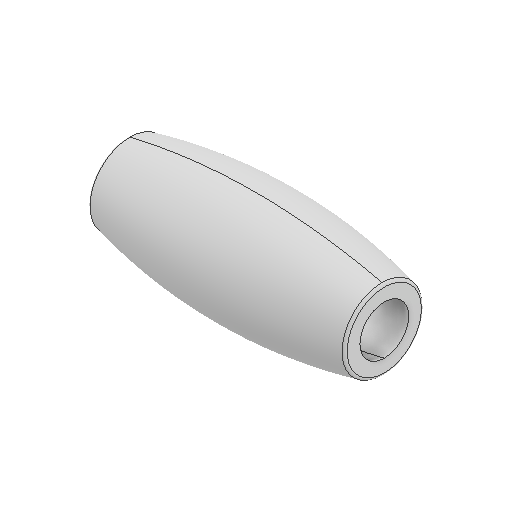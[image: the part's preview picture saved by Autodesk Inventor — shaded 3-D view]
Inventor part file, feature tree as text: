
AUTODESK INVENTOR PART (.ipt)
format: ipt  version: 2024.1 (Build 281209000, 209)  size: 181,248 bytes
history: native  units: in
note: dims shown in document units (in); Inventor stores cm internally (conversion verified against a paired STEP export)
features: fillet x1
ambient origin geometry x8: Origin, YZ Plane, XZ Plane, XY Plane, X Axis, Y Axis, Z Axis, Center Point
bodies: Solid1 (feature_tree)
feature tree (1):
  fillet  "Fillet1"  [1 undecoded]
note: 1 required parameter value undecoded (feature->parameter linkage not recoverable at this tier; creation-order binding heuristic only, values carry confidence <= 0.55)
